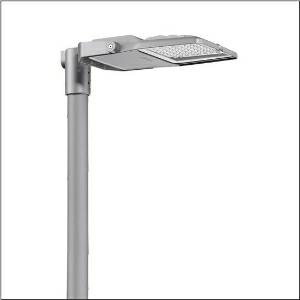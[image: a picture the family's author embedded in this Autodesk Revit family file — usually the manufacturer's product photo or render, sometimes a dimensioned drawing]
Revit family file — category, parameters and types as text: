
# Revit family: floodlight_fl_21_iq_mini___pl52_5xa7771d2d3a_64cb
name_source: partatom
category: Lighting Fixtures
units: mm (PartAtom-declared; Revit-internal decimal feet)

## family parameters
Cut with Voids When Loaded = No
Host = Face
Light Source = No
Part Type = Normal
Room Calculation Point = No
Round Connector Dimension = Use Diameter
Shared = No

## types (1)
- --- (1 x LED, 17830 lm, 143 W, 3000K)
    Apparent Load = 143 VA
    CIE Flux Codes = 26 60 98 100 100
    Color Rendering = 70
    Color Temperature = 3000K
    Default Elevation = 1800 mm
    Description = Floodlight FL 21 iQ mini, floodlight, primary light control with lens, of PMMA, primary optical cover: protective disc, of toughened safety glass, transparent, light distribution: PL52, light emission: direct distribution, installation type: surface-mounted, lamps: LED, High Power LED, rated values: 17.830lm | 143W | 124,7lm/W (begin service life); end service life: 17.830lm | 151,6W; at 50% lumin. flux: 8.915lm | 60,6W | 147,1lm/W, colour temperature: 3000K, colour rendering: CRI > 70, light colour: 730, light setting 1 begin service life: 100% | 17.830lm | 143W | 124,7lm/W | 3.000K, light setting 1 end service life: 151,6W, further light settings possible, control: Auto-Match, Temp-Guard, Lumen-Switch, Night-Set, Smart-Wire, Light-Fading, Desk-Remote (wireless, voltage-free reading and setting of iQ features in the workshop via application-optimized NFC function/RFID function), optimised constant luminous flux control (CLO 2.0), pre-setting: linear dimming characteristic, with terminal, 6-pole, mains connection: 220..240V, AC, 50/60Hz, luminaire housing, of diecast aluminium, powder-coated, SITECO metallic grey (DB 702S), corrosivity category C5 mid according to DIN EN ISO 12944suitable for swimming poolschlorine-resistant, sealing non-destructively replaceable, please order mast flange separately, mast bracket, of steel, galvanised, powder-coated, SITECO metallic grey (DB 702S), protection rating (complete): IP66, insulation class (complete): insulation class II (safety insulation), certification: CE, ENEC, VDE, protection symbol: D, impact resistance: IK08, permissible operating ambient temperature: -40..+40°C, permissible operating ambient temperature for outdoor applications: -40..+50°C, standard: DIN EN 12944, LABS conformity tested according to VDMA 24364:2018-05, packaging unit: 1 piece

Light Distribution: PL52
    Height = 70 mm
    Lamp = 1 x LED
    Lamp Light Flux = 17830 lm
    Lamp Power = 143 W
    Lamp count = 1
    Length = 485 mm
    Luminous efficacy = 125 lm/W
    Manufacturer = Siteco
    ModVariant = No
    Model = 5XA7771D2D3A
    Number of Poles = 1
    OnlyDefault = Yes
    Power Factor = 1
    Product Name = Floodlight FL 21 iQ mini | PL52
    Product group = floodlight | pylon annexe
    ProductGroupID = 6201
    Protection Class = Protection class II
    Protection Degree = IP 66
    RLX_Detail_Level = 1
    RLX_Emergency_Light_Flux = 0 lm
    RLX_Emergency_Type = 0
    RLX_Emergency_Type_DB = No
    RlxData = <blob elided: 101917 chars, md5=6d148339>
    Socket = socket
    Standby Power = 0 W
    System Light Flux = 17830 lm
    System Power = 143 W
    Type Comments = factory setting: luminous flux: 100 % | dim-lin: 254 | 730 mA
    Type Image = l_1007125.jpg
    URL = http://relux.com
    VarID = @adj_163447
    Voltage = 0 V
    Weight = 0.00 kg
    Width = 337 mm

## geometry (parser evidence)
native form markers: Blend x4, Sweep x13
no freeform markers — native parametric forms only
